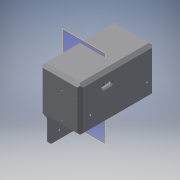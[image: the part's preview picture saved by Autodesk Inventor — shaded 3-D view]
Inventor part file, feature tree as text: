
AUTODESK INVENTOR PART (.ipt)
format: ipt  version: 2018 (Build 220112000, 112)  size: 315,904 bytes
history: native  units: mm
features: extrude x9, reference x9, sketch x8, other x5, chamfer x4, fillet x2, shell x1, plane x1, mirror x1
ambient origin geometry x8: Origin, YZ Plane, XZ Plane, XY Plane, X Axis, Y Axis, Z Axis, Center Point
bodies: Solid1 (feature_tree)
feature tree (40):
  extrude  "Extrusion1"  Depth=7.0mm
  shell  "Shell1"  Thickness=5.5mm
  extrude  "Extrusion10"  Depth=2.4mm TaperAngle=0.0deg
  sketch  "Sketch3"  dims[d9=5.5mm d12=2.4mm d13=0.0mm]
  extrude  "Extrusion11"  Depth=45.0mm TaperAngle=0.0deg
  extrude  "Extrusion4"  Depth=7.0mm TaperAngle=45.0deg
  extrude  "Extrusion6"  Depth=15.0mm
  extrude  "Extrusion5"  Depth=45.0mm TaperAngle=0.0deg
  fillet  "Fillet1"  Radius=5.5mm
  chamfer  "Chamfer1"  Distance=2.4mm
  chamfer  "Chamfer2"  Distance=22.0mm
  extrude  "Extrusion7"  Depth=0.5mm TaperAngle=0.0deg
  plane  "Work Plane1"
  extrude  "Extrusion8"  Depth=0.5mm TaperAngle=45.0deg
  mirror  "Mirror1"
  extrude  "Extrusion9"  Depth=10.0mm TaperAngle=0.0deg
  chamfer  "Chamfer3"  Distance=2.4mm
  fillet  "Fillet2"  Radius=1.0mm
  chamfer  "Chamfer4"  Distance=5.0mm Angle=45.0deg
  sketch  "Sketch1"  dims[d1=15.0mm d2=55.0mm d3=0.0mm d4=0.0mm d5=7.0mm d8=5.5mm]
  reference  "Reference1"
  sketch  "Sketch5"  dims[d14=2.4mm d15=0.0mm d16=45.0mm d17=0.0mm]
  reference  "Reference15"
  sketch  "Sketch6"  dims[d18=7.0mm d19=5.0mm d20=2.0mm d21=45.0deg]
  reference  "Reference16"
  sketch  "Sketch8"  dims[d22=5.0mm d23=2.0mm d24=45.0deg d25=15.0mm]
  sketch  "Sketch9"  dims[d26=3.0mm d27=45.0mm d28=0.0mm d29=5.5mm d30=2.4mm d31=0.0mm]
  sketch  "Sketch10"  dims[d33=15.0mm]
  sketch  "Sketch11"  dims[d34=3.0mm d35=22.0mm d36=2.4mm d37=0.0mm d38=2.0mm d39=2.0mm d40=45.0deg d41=10.0mm d42=0.0mm d43=2.4mm d44=0.0mm d45=1.0mm d46=5.0mm d47=2.0mm d48=45.0deg d49=1.8mm d50=29.5mm d51=21.5mm d52=1.075mm d53=3.0mm d54=0.5mm]
  reference  "Reference17"
  reference  "Reference18"
  reference  "Reference20"
  reference  "Reference21"
  reference  "Reference22"
  reference  "Reference23"
  other  "<userpath>\Downloads\git_WSL\MEME_MACHINE\CAD\PSU Case\PSU Case.iam"
  other  "PSU Case.iam"
  other  "PSU:1"
  other  "Switch:1"
  other  "C14 Connector:1"
